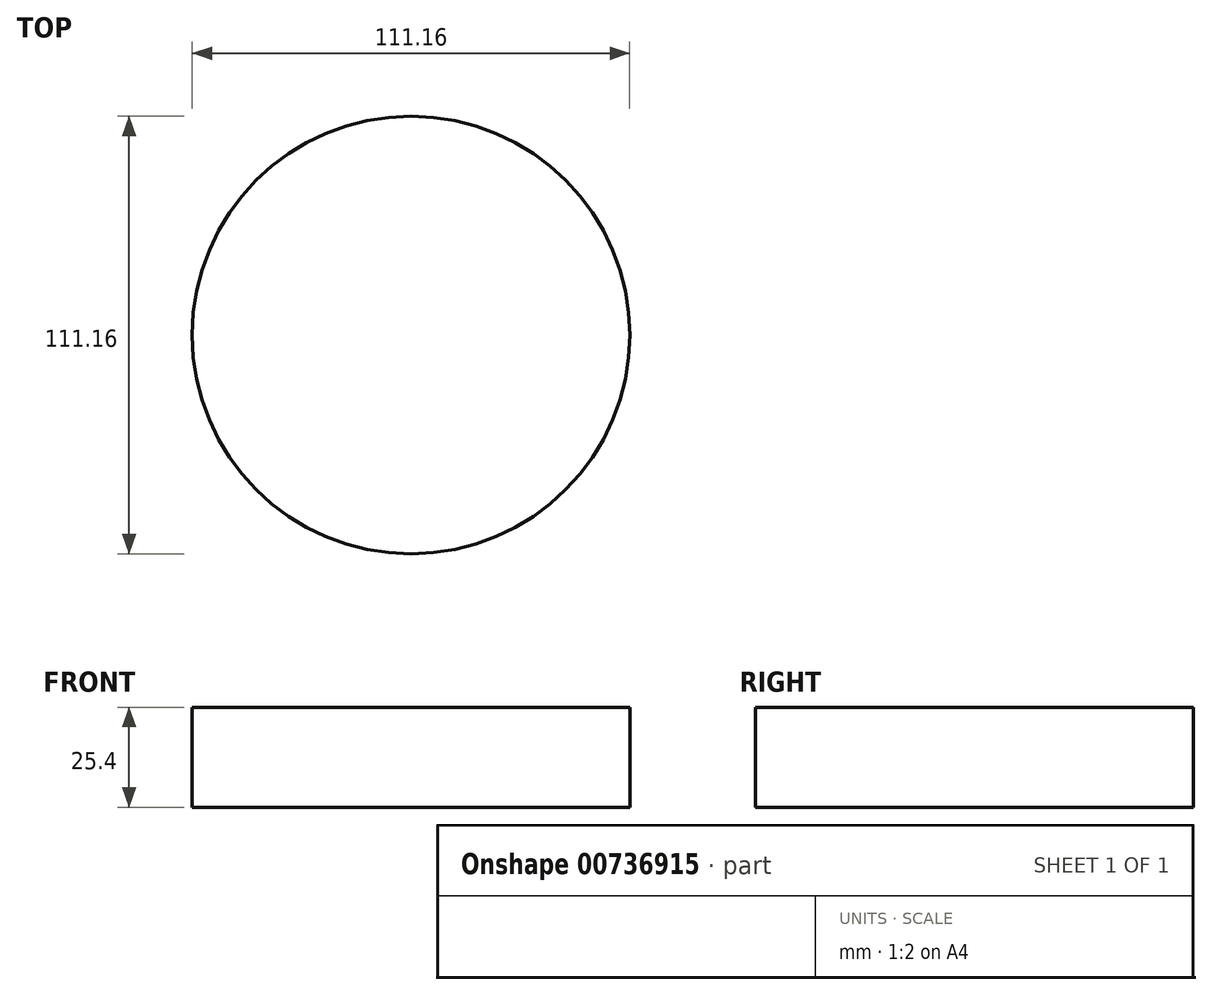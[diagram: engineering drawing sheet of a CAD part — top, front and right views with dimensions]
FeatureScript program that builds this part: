
annotation { "Feature Type Name" : "Feature", "Feature Type Description" : "" }
export const myFeature = defineFeature(function(context is Context, id is Id, definition is map)
    precondition{}
    {
        {
            var Q0;
            Q0=qCreatedBy(makeId("Top.planeOp"),FACE);
            var sketch = newSketch(context, id + "F0", { "sketchPlane" : qUnion([Q0])});
            skCircle(sketch, "E0", {"center": v(0, 0) * mm, "radius": 55.58 * mm});
            skSolve(sketch);
        }
        {
            var Q0;
            Q0=makeQuery(id+"F0.imprint","IMPRINT",FACE,{"disambiguationData":[TD([[makeQuery(id+"F0.imprint","IMPRINT",EDGE,{"derivedFrom":sQuery(id+"F0.wireOp",EDGE,"E0")}),1.0]])]});
            extrude(context, id + "F1", {"entities" : qUnion([Q0]), "depth" : 25.4 * mm, "offsetDistance" : 25.4 * mm});
        }
    });
